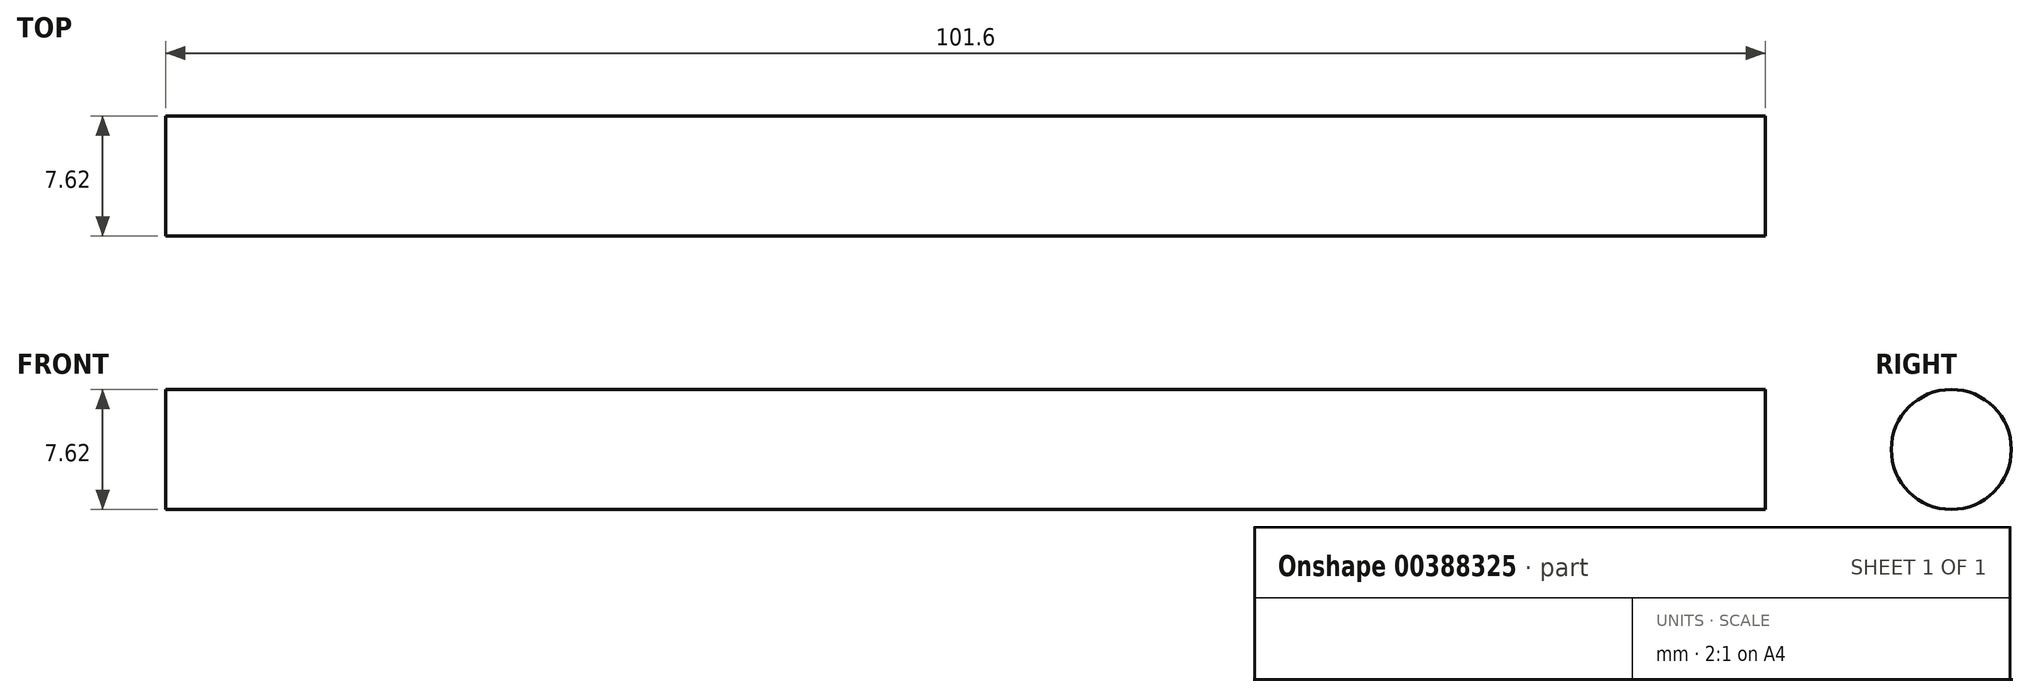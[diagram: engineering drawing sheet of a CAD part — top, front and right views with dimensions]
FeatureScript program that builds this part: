
annotation { "Feature Type Name" : "Feature", "Feature Type Description" : "" }
export const myFeature = defineFeature(function(context is Context, id is Id, definition is map)
    precondition{}
    {
        {
            var Q0;
            Q0=qCreatedBy(makeId("Front.planeOp"),FACE);
            var sketch = newSketch(context, id + "F0", { "sketchPlane" : qUnion([Q0])});
            skLineSegment(sketch, "E0", {"start": v(-27.11, 0) * mm, "end": v(74.49, 0) * mm});
            skLineSegment(sketch, "E1", {"start": v(74.49, 0) * mm, "end": v(74.49, -3.8) * mm});
            skLineSegment(sketch, "E2", {"start": v(74.49, -3.8) * mm, "end": v(-27.11, -3.81) * mm});
            skLineSegment(sketch, "E3", {"start": v(-27.11, -3.81) * mm, "end": v(-27.11, 0) * mm});
            skSolve(sketch);
        }
        {
            var Q0;
            Q0 = qSketchRegion(id + "F0", true);
            var Q1;
            Q1=sQuery(id+"F0.wireOp",EDGE,"E2");
            revolve(context, id + "F1", {"entities" : qUnion([Q0]), "axis" : qUnion([Q1]), "revolveType" : RevolveType.FULL});
        }
    });
